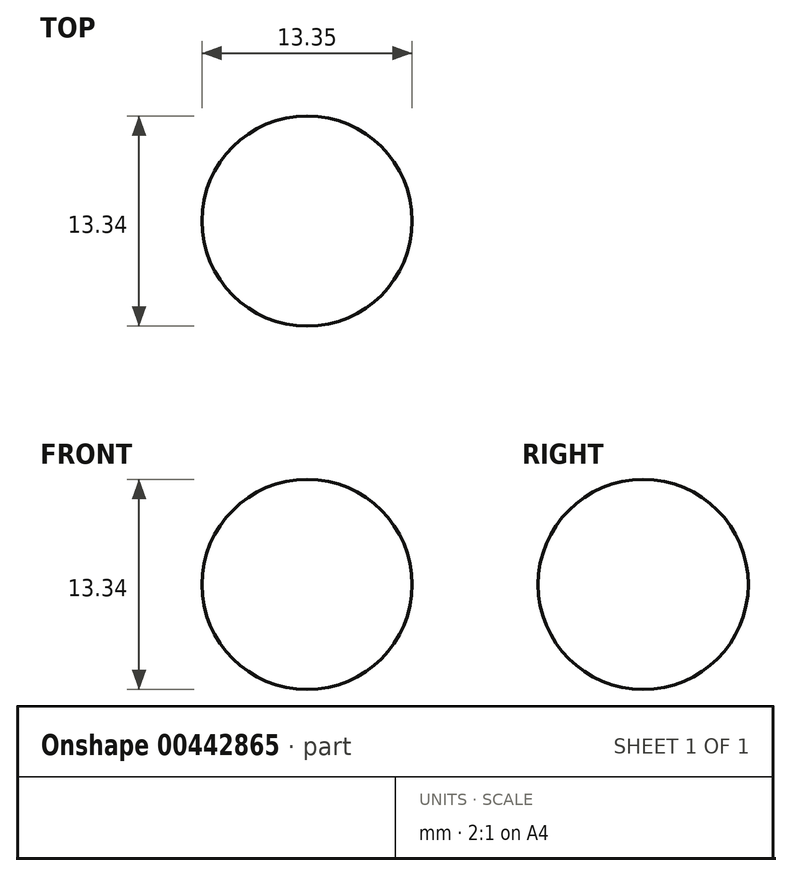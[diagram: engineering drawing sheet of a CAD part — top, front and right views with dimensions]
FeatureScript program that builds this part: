
annotation { "Feature Type Name" : "Feature", "Feature Type Description" : "" }
export const myFeature = defineFeature(function(context is Context, id is Id, definition is map)
    precondition{}
    {
        {
            var Q0;
            Q0=qCreatedBy(makeId("Front.planeOp"),FACE);
            var sketch = newSketch(context, id + "F0", { "sketchPlane" : qUnion([Q0])});
            skArc(sketch, "E0", {"start": v(2.12, 6.67) * mm, "mid": v(-4.55, 0) * mm, "end": v(2.12, -6.67) * mm});
            skLineSegment(sketch, "E1", {"start": v(2.12, -6.67) * mm, "end": v(2.12, 6.67) * mm});
            skSolve(sketch);
        }
        {
            var Q0;
            Q0 = qSketchRegion(id + "F0", true);
            var Q1;
            Q1=sQuery(id+"F0.wireOp",EDGE,"E1");
            revolve(context, id + "F1", {"entities" : qUnion([Q0]), "axis" : qUnion([Q1]), "revolveType" : RevolveType.FULL});
        }
    });
